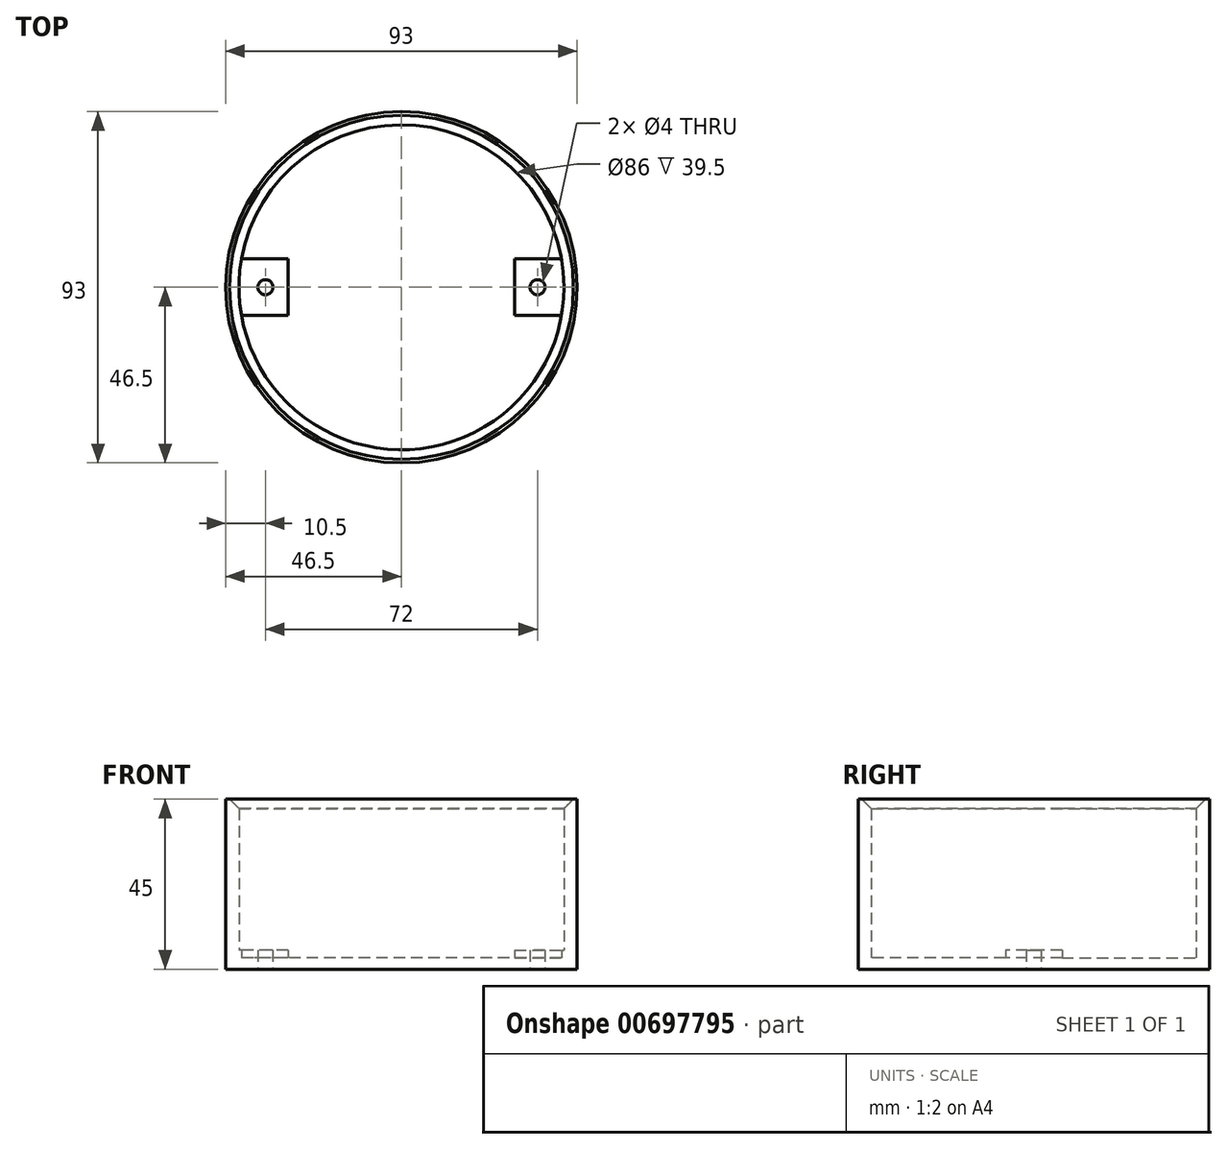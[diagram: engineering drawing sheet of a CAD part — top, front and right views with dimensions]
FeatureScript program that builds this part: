
annotation { "Feature Type Name" : "Feature", "Feature Type Description" : "" }
export const myFeature = defineFeature(function(context is Context, id is Id, definition is map)
    precondition{}
    {
        {
            var Q0;
            Q0=qCreatedBy(makeId("Top.planeOp"),FACE);
            var sketch = newSketch(context, id + "F0", { "sketchPlane" : qUnion([Q0])});
            skCircle(sketch, "E0", {"center": v(0, 0) * mm, "radius": 46.5 * mm});
            skCircle(sketch, "E1", {"center": v(-36, 0) * mm, "radius": 2 * mm});
            skCircle(sketch, "E2", {"center": v(36, 0) * mm, "radius": 2 * mm});
            skSolve(sketch);
        }
        {
            var Q0;
            Q0=makeQuery(id+"F0.imprint","IMPRINT",FACE,{"disambiguationData":[TD([[makeQuery(id+"F0.imprint","IMPRINT",EDGE,{"derivedFrom":sQuery(id+"F0.wireOp",EDGE,"E0")}),1.0]])]});
            extrude(context, id + "F1", {"entities" : qUnion([Q0]), "depth" : 3 * mm, "offsetDistance" : 25 * mm});
        }
        {
            var Q0;
            Q0=makeQuery(id+"F1.opExtrude","CAP_FACE",FACE,{"disambiguationData":[OSD([sQuery(id+"F0.wireOp",EDGE,"E0"),sQuery(id+"F0.wireOp",EDGE,"E1"),sQuery(id+"F0.wireOp",EDGE,"E2")])],"isStart":false});
            var sketch = newSketch(context, id + "F2", { "sketchPlane" : qUnion([Q0])});
            skCircle(sketch, "E3", {"center": v(0, 0) * mm, "radius": 43 * mm});
            skCircle(sketch, "E4", {"center": v(0, 0) * mm, "radius": 46.5 * mm});
            skSolve(sketch);
        }
        {
            var Q0;
            Q0=makeQuery(id+"F2.imprint","IMPRINT",FACE,{"disambiguationData":[TD([[makeQuery(id+"F2.imprint","IMPRINT",EDGE,{"derivedFrom":sQuery(id+"F2.wireOp",EDGE,"E3")}),-1.0]])]});
            extrude(context, id + "F3", {"entities" : qUnion([Q0]), "operationType" : NewBodyOperationType.ADD, "depth" : 42 * mm, "offsetDistance" : 25 * mm});
        }
        {
            var Q0;
            Q0=makeQuery(id+"F3.opExtrude","CAP_EDGE",EDGE,{"disambiguationData":[OSD([sQuery(id+"F2.wireOp",EDGE,"E3")])],"isStart":false});
            chamfer(context, id + "F4", {"entities" : qUnion([Q0]), "width" : 2.5 * mm, "tangentPropagation" : true});
        }
        {
            var Q0;
            Q0=makeQuery(id+"F1.opExtrude","CAP_FACE",FACE,{"disambiguationData":[OSD([sQuery(id+"F0.wireOp",EDGE,"E0"),sQuery(id+"F0.wireOp",EDGE,"E1"),sQuery(id+"F0.wireOp",EDGE,"E2")])],"isStart":false});
            var sketch = newSketch(context, id + "F5", { "sketchPlane" : qUnion([Q0])});
            skLineSegment(sketch, "E5", {"start": v(-30, 7.5) * mm, "end": v(-30, -7.5) * mm});
            skLineSegment(sketch, "E6", {"start": v(-30, 7.5) * mm, "end": v(-42.34, 7.5) * mm});
            skLineSegment(sketch, "E7", {"start": v(-30, -7.5) * mm, "end": v(-42.34, -7.5) * mm});
            skArc(sketch, "E8", {"start": v(-42.34, 7.5) * mm, "mid": v(-43, 0) * mm, "end": v(-42.34, -7.5) * mm});
            skLineSegment(sketch, "E9.MirrorCS", {"start": v(30, 7.5) * mm, "end": v(30, -7.5) * mm});
            skLineSegment(sketch, "E10.MirrorCS", {"start": v(30, 7.5) * mm, "end": v(42.34, 7.5) * mm});
            skLineSegment(sketch, "E11.MirrorCS", {"start": v(30, -7.5) * mm, "end": v(42.34, -7.5) * mm});
            skArc(sketch, "E12.MirrorCS", {"start": v(42.34, 7.5) * mm, "mid": v(43, 0) * mm, "end": v(42.34, -7.5) * mm});
            skSolve(sketch);
        }
        {
            var Q0;
            Q0=makeQuery(id+"F5.imprint","IMPRINT",FACE,{"disambiguationData":[TD([[makeQuery(id+"F5.imprint","IMPRINT",EDGE,{"derivedFrom":sQuery(id+"F5.wireOp",EDGE,"E5")}),-1.0]])]});
            var Q1;
            Q1=makeQuery(id+"F5.imprint","IMPRINT",FACE,{"disambiguationData":[TD([[makeQuery(id+"F5.imprint","IMPRINT",EDGE,{"derivedFrom":sQuery(id+"F5.wireOp",EDGE,"E9.MirrorCS")}),1.0]])]});
            extrude(context, id + "F6", {"entities" : qUnion([Q0, Q1]), "operationType" : NewBodyOperationType.ADD, "depth" : 2 * mm, "offsetDistance" : 25 * mm});
        }
    });
